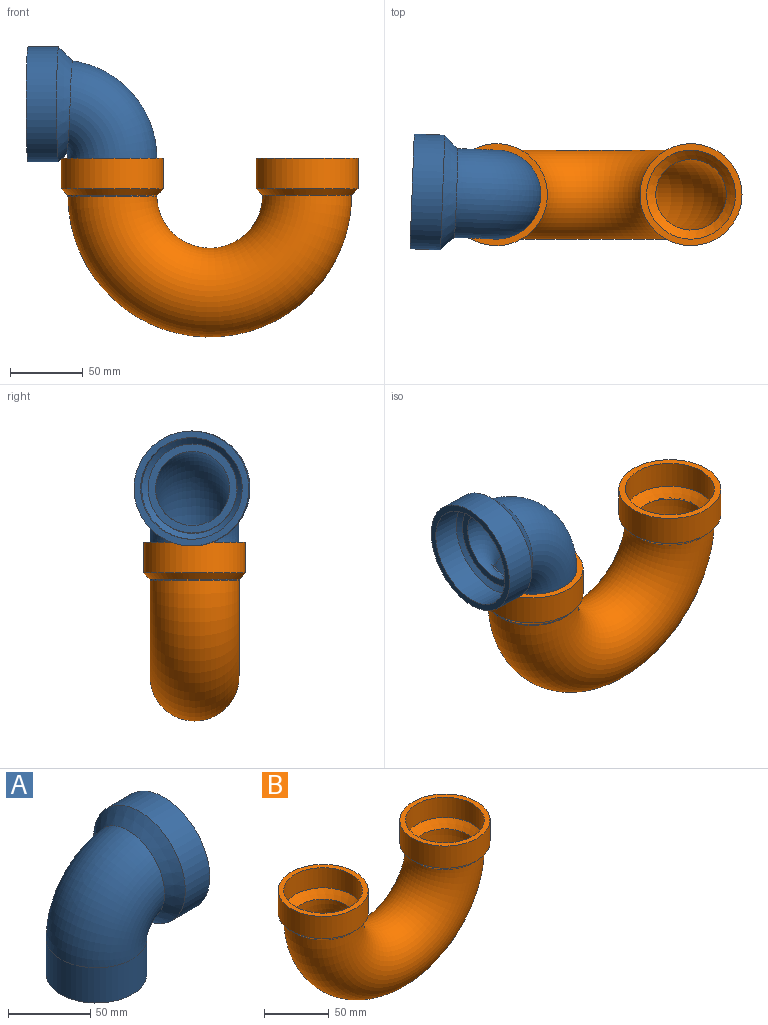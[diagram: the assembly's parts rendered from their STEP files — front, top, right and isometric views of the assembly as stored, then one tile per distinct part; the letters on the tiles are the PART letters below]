
ASSEMBLY  parts=2 mates=1
PART A: 14 faces, bbox 93.8x78.7x102.4 mm
  f0: torus R=36.83mm, axis (0,1,0), area 454.5mm2, adj f5,f12
  f1: plane 60.96x60.96mm, normal (0,0,-1), area 891.8mm2, adj f2,f3
  f2: cylinder r=30.48mm len=60.96mm, axis (0,0,-1), area 5010.3mm2, adj f1,f4
  f3: cylinder r=25.4mm len=50.8mm, axis (0,0,-1), area 4175.3mm2, adj f1,f6
  f4: torus R=36.83mm, axis (0,1,0), area 9431.4mm2, adj f2,f9
  f5: plane 60.96x60.96mm, normal (1,0,0), area 891.8mm2, adj f0,f6
  f6: torus R=36.83mm, axis (0,1,0), area 9213.7mm2, adj f3,f5,f7,f8
  f7: cylinder r=29.21mm len=23.56mm, axis (-1,0,0), area 26.6mm2, adj f6,f8
  f8: cone r=29.21mm half-angle=45deg, axis (1,0,0), area 20.2mm2, adj f6,f7
  f9: cone r=29.21mm half-angle=45deg, axis (1,0,0), area 2614.9mm2, adj f4,f11
  f10: plane 78.74x78.74mm, normal (1,0,0), area 1065.3mm2, adj f11,f13
  f11: cylinder r=39.37mm len=78.74mm, axis (-1,0,0), area 5183.6mm2, adj f9,f10
  f12: cone r=29.21mm half-angle=45deg, axis (1,0,0), area 1236.4mm2, adj f0,f13
  f13: cylinder r=34.8mm len=69.6mm, axis (-1,0,0), area 4167.6mm2, adj f10,f12
PART B: 14 faces, bbox 210.3x69.9x130.6 mm
  f0: torus R=66.67mm, axis (0,-1,0), area 33429.2mm2, adj f2,f8
  f1: torus R=66.67mm, axis (0,-1,0), area 40115.1mm2, adj f7,f13
  f2: plane 50.8x50.8mm, normal (0,0,-1), area 187.9mm2, adj f0,f6
  f3: cylinder r=34.92mm len=69.85mm, axis (0,0,-1), area 4598.4mm2, adj f4,f7
  f4: plane 69.85x69.85mm, normal (0,0,1), area 913.3mm2, adj f3,f5
  f5: cylinder r=30.48mm len=60.96mm, axis (0,0,-1), area 3660.5mm2, adj f4,f6
  f6: cone r=24.19mm half-angle=45deg, axis (0,0,1), area 1527mm2, adj f2,f5
  f7: cone r=34.92mm half-angle=45deg, axis (0,0,1), area 1291.7mm2, adj f1,f3
  f8: plane 50.8x50.8mm, normal (0,0,-1), area 187.9mm2, adj f0,f12
  f9: cylinder r=34.92mm len=69.85mm, axis (0,0,-1), area 4598.4mm2, adj f10,f13
  f10: plane 69.85x69.85mm, normal (0,0,1), area 913.3mm2, adj f9,f11
  f11: cylinder r=30.48mm len=60.96mm, axis (0,0,-1), area 3660.5mm2, adj f10,f12
  f12: cone r=24.19mm half-angle=45deg, axis (0,0,1), area 1527mm2, adj f8,f11
  f13: cone r=34.92mm half-angle=45deg, axis (0,0,1), area 1291.7mm2, adj f1,f9
PLACE A rot(axis=(0,0,1),177.9deg) t=(-137.15,11.93,4.72)mm
PLACE B t=(-3.85,9.45,11.77)mm fixed
MATE revolute B.f3 <-> A.f2  axis (0,0,1) through (-70.52,9.45,37.17)mm
